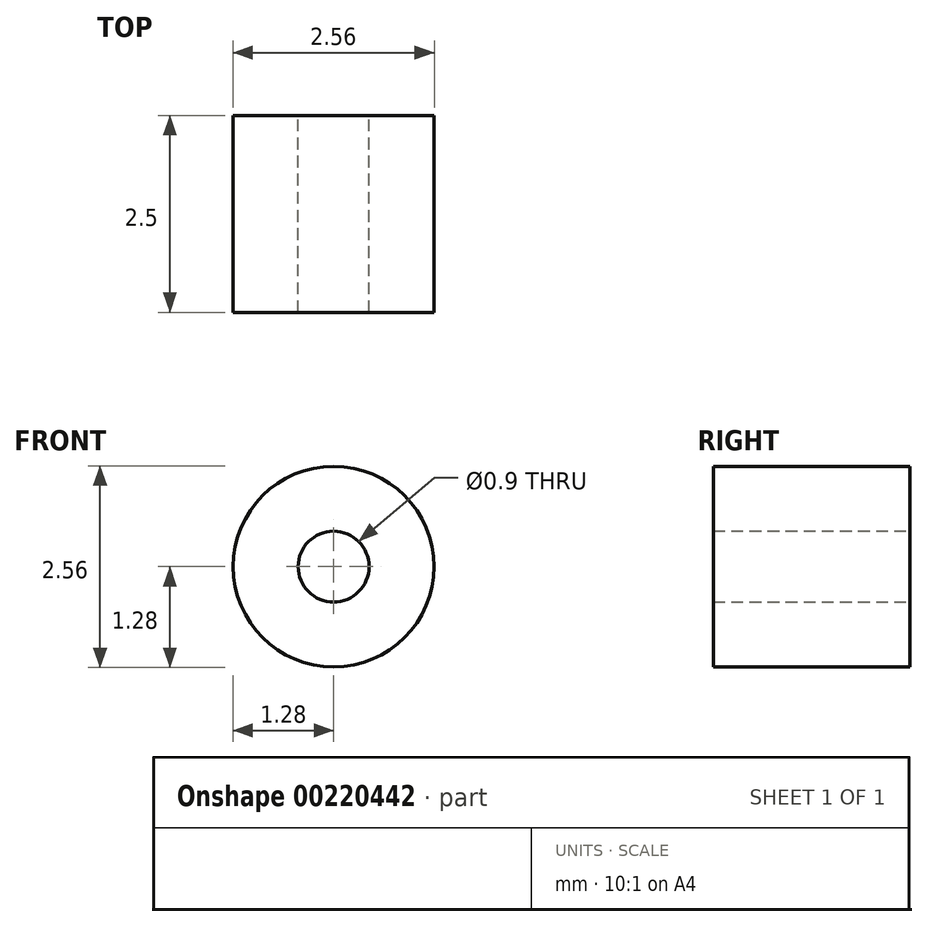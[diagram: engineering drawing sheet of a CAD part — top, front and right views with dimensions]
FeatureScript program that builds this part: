
annotation { "Feature Type Name" : "Feature", "Feature Type Description" : "" }
export const myFeature = defineFeature(function(context is Context, id is Id, definition is map)
    precondition{}
    {
        {
            var Q0;
            Q0=qCreatedBy(makeId("Front.planeOp"),FACE);
            var sketch = newSketch(context, id + "F0", { "sketchPlane" : qUnion([Q0])});
            skCircle(sketch, "E0", {"center": v(0, 0) * mm, "radius": 1.27 * mm});
            skCircle(sketch, "E1", {"center": v(0, 0) * mm, "radius": 0.45 * mm});
            skSolve(sketch);
        }
        {
            var Q0;
            Q0=makeQuery(id+"F0.imprint","IMPRINT",FACE,{"disambiguationData":[TD([[makeQuery(id+"F0.imprint","IMPRINT",EDGE,{"derivedFrom":sQuery(id+"F0.wireOp",EDGE,"E0")}),1.0]])]});
            extrude(context, id + "F1", {"entities" : qUnion([Q0]), "depth" : 2.5 * mm});
        }
    });
